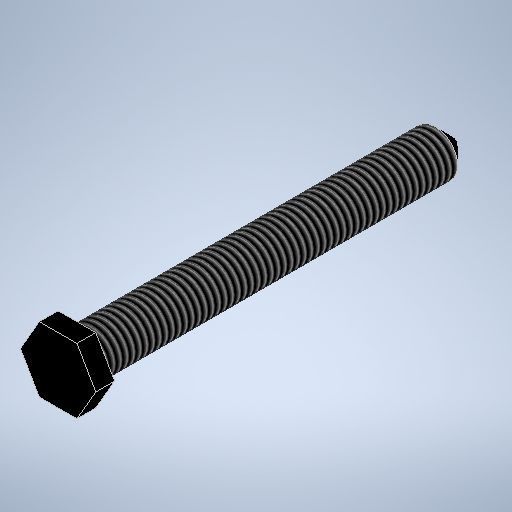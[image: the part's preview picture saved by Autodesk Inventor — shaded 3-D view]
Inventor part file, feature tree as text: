
AUTODESK INVENTOR PART (.ipt)
format: ipt  version: 2025.2 (Build 292293000, 293)  size: 289,280 bytes
history: native  units: mm
features: extrude x2, chamfer x2, sketch x2, other x1, thread x1
ambient origin geometry x8: Origin, YZ Plane, XZ Plane, XY Plane, X Axis, Y Axis, Z Axis, Center Point
bodies: Body1 (feature_tree)
feature tree (8):
  other  "Sólido1"
  extrude  "Extrusão1"  Depth=100.0mm TaperAngle=0.0deg
  extrude  "Extrusão2"  Depth=5.0mm TaperAngle=0.0deg
  thread  "Rosca1"  [1 undecoded]
  chamfer  "Chanfro1"  Distance=2.0mm Angle=45.0deg
  chamfer  "Chanfro2"  Distance=5.0mm Angle=45.0deg
  sketch  "Esboço1"  dims[d0=12.0mm d1=100.0mm d2=0.0mm]
  sketch  "Esboço2"  dims[d3=10.0mm d4=5.0mm d5=0.0mm d6=100.0mm d7=0.0mm d8=2.0mm d9=2.0mm d10=45.0deg d11=5.0mm d12=2.0mm d13=45.0deg]
note: 1 required parameter value undecoded (feature->parameter linkage not recoverable at this tier; creation-order binding heuristic only, values carry confidence <= 0.55)
